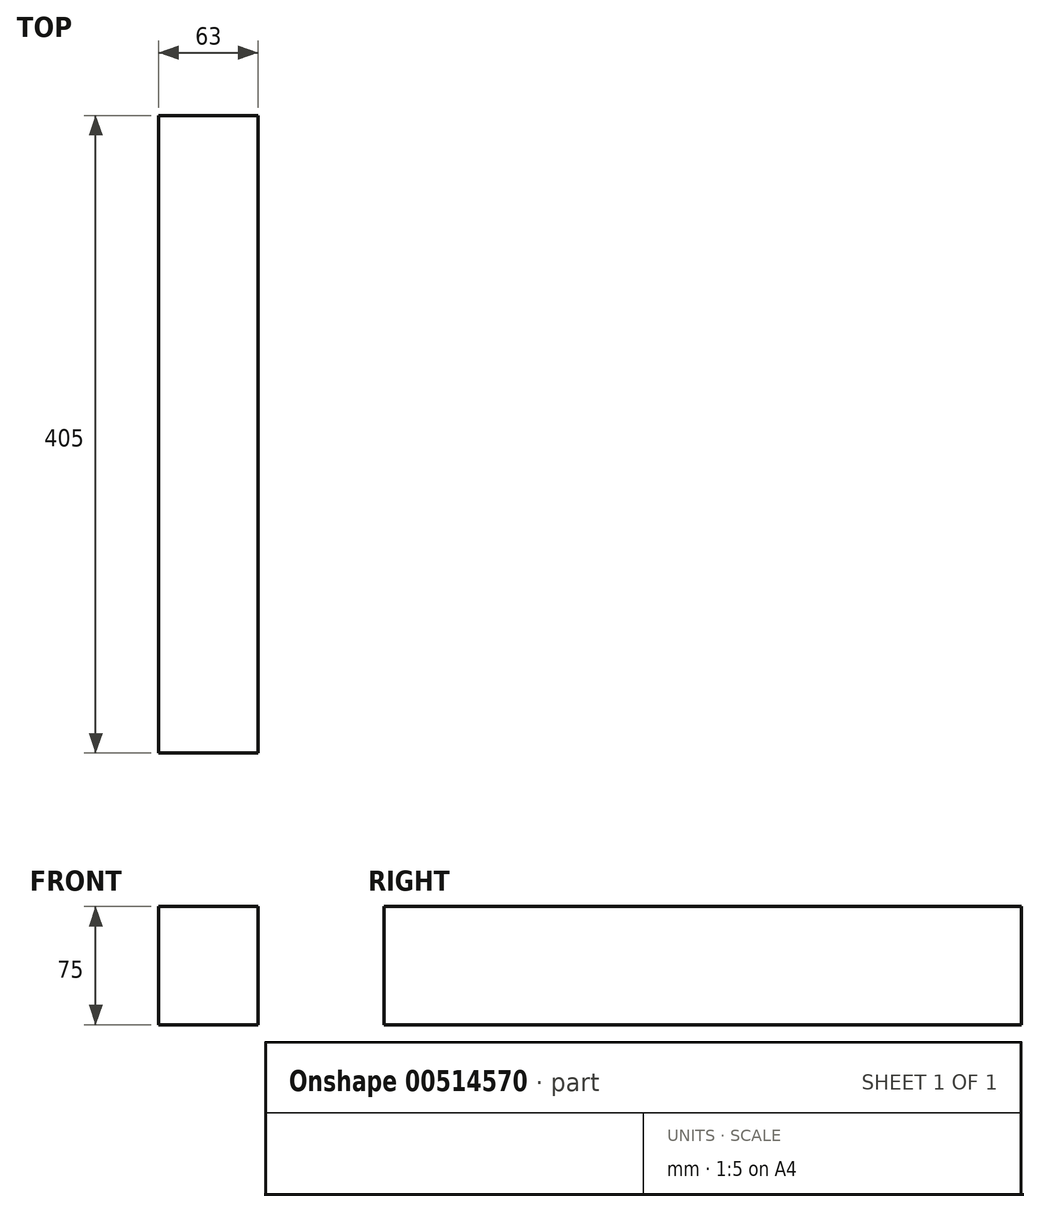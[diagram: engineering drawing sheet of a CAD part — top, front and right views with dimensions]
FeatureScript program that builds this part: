
annotation { "Feature Type Name" : "Feature", "Feature Type Description" : "" }
export const myFeature = defineFeature(function(context is Context, id is Id, definition is map)
    precondition{}
    {
        {
            var Q0;
            Q0=qCreatedBy(makeId("Front.planeOp"),FACE);
            var sketch = newSketch(context, id + "F0", { "sketchPlane" : qUnion([Q0])});
            skLineSegment(sketch, "E0.bottom", {"start": v(31.5, 37.5) * mm, "end": v(-31.5, 37.5) * mm});
            skLineSegment(sketch, "E0.top", {"start": v(31.5, -37.5) * mm, "end": v(-31.5, -37.5) * mm});
            skLineSegment(sketch, "E0.left", {"start": v(31.5, 37.5) * mm, "end": v(31.5, -37.5) * mm});
            skLineSegment(sketch, "E0.right", {"start": v(-31.5, 37.5) * mm, "end": v(-31.5, -37.5) * mm});
            skPoint(sketch, "E0.middle", {"position": v(0, 0) * mm});
            skSolve(sketch);
        }
        {
            var Q0;
            Q0=qSketchRegion(id+"F0",true);
            extrude(context, id + "F1", {"entities" : qUnion([Q0]), "depth" : (600 - 195) * mm, "offsetDistance" : 25 * mm});
        }
    });
